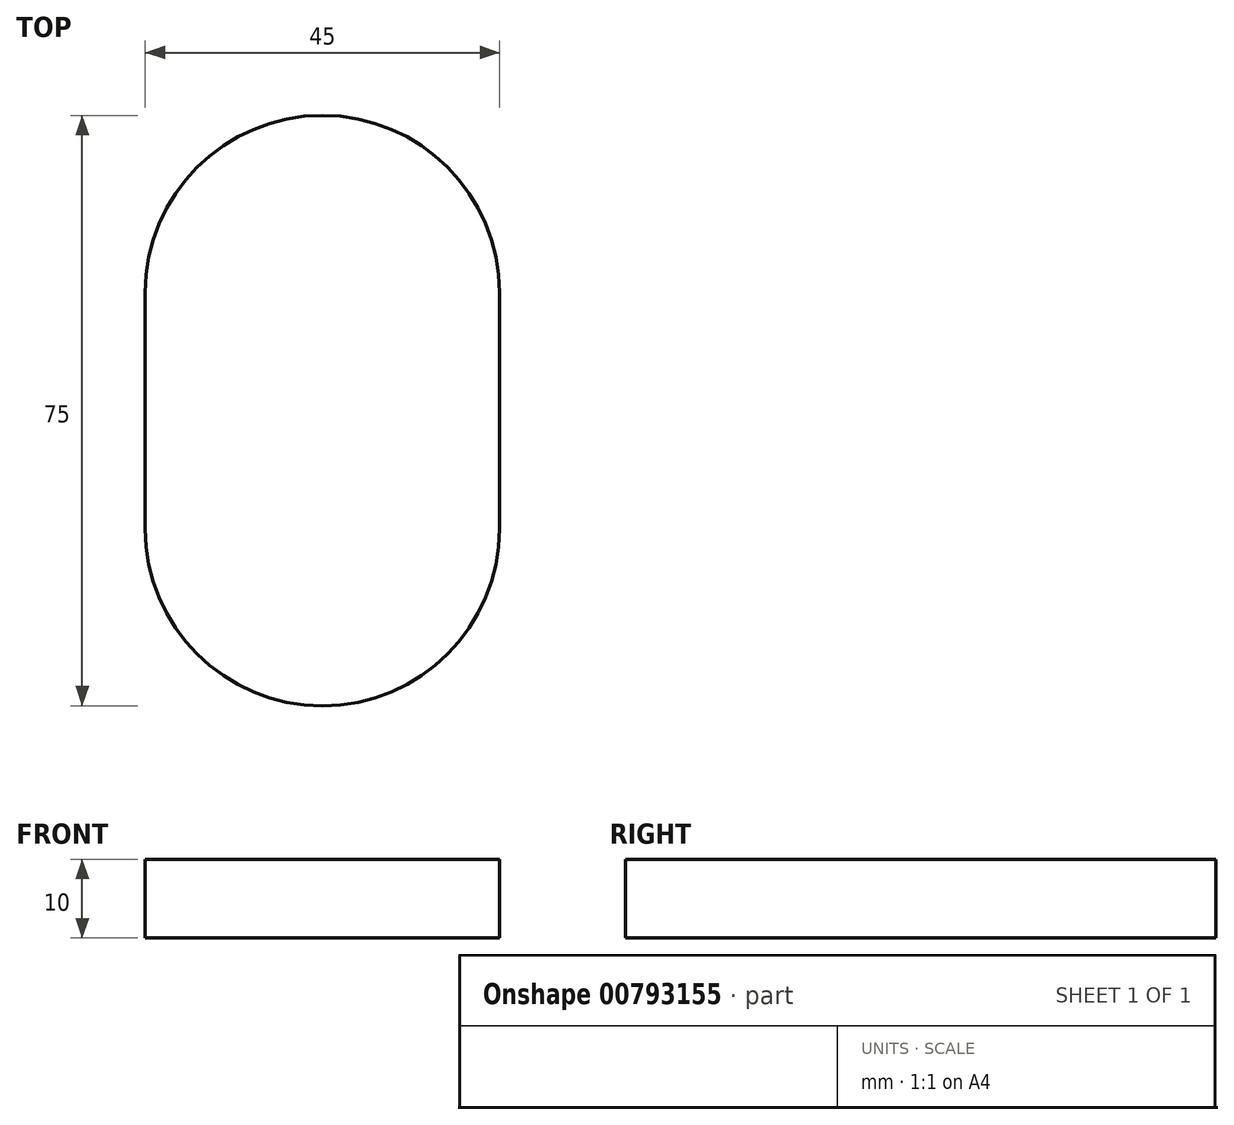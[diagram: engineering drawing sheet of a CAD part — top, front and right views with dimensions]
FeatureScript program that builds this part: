
annotation { "Feature Type Name" : "Feature", "Feature Type Description" : "" }
export const myFeature = defineFeature(function(context is Context, id is Id, definition is map)
    precondition{}
    {
        {
            var Q0;
            Q0=qCreatedBy(makeId("Top.planeOp"),FACE);
            var sketch = newSketch(context, id + "F0", { "sketchPlane" : qUnion([Q0])});
            skLineSegment(sketch, "E0", {"start": v(0, 15) * mm, "end": v(0, -15) * mm, "construction": true});
            skArc(sketch, "E1.0.startCap", {"start": v(-22.5, 15) * mm, "mid": v(0, 37.5) * mm, "end": v(22.5, 15) * mm});
            skArc(sketch, "E1.0.endCap", {"start": v(22.5, -15) * mm, "mid": v(0, -37.5) * mm, "end": v(-22.5, -15) * mm});
            skLineSegment(sketch, "E1.0.left", {"start": v(22.5, 15) * mm, "end": v(22.5, -15) * mm});
            skLineSegment(sketch, "E1.0.right", {"start": v(-22.5, 15) * mm, "end": v(-22.5, -15) * mm});
            skLineSegment(sketch, "E2.bottom", {"start": v(57.5, 80) * mm, "end": v(-57.5, 80) * mm});
            skLineSegment(sketch, "E2.top", {"start": v(57.5, -80) * mm, "end": v(-57.5, -80) * mm});
            skLineSegment(sketch, "E2.left", {"start": v(57.5, 80) * mm, "end": v(57.5, -80) * mm});
            skLineSegment(sketch, "E2.right", {"start": v(-57.5, 80) * mm, "end": v(-57.5, -80) * mm});
            skPoint(sketch, "E2.middle", {"position": v(0, 0) * mm});
            skSolve(sketch);
        }
        {
            var Q0;
            Q0=makeQuery(id+"F0.imprint","IMPRINT",FACE,{"disambiguationData":[TD([[makeQuery(id+"F0.imprint","IMPRINT",EDGE,{"derivedFrom":sQuery(id+"F0.wireOp",EDGE,"E1.0.startCap")}),1.0]])]});
            extrude(context, id + "F1", {"entities" : qUnion([Q0]), "depth" : 10 * mm, "offsetDistance" : 25 * mm});
        }
        {
            var Q0;
            Q0=makeQuery(id+"F1.opExtrude","CAP_FACE",FACE,{"disambiguationData":[OSD([sQuery(id+"F0.wireOp",EDGE,"E1.0.startCap"),sQuery(id+"F0.wireOp",EDGE,"E1.0.endCap"),sQuery(id+"F0.wireOp",EDGE,"E1.0.left"),sQuery(id+"F0.wireOp",EDGE,"E1.0.right"),sQuery(id+"F0.wireOp",EDGE,"E2.bottom"),sQuery(id+"F0.wireOp",EDGE,"E2.top"),sQuery(id+"F0.wireOp",EDGE,"E2.left"),sQuery(id+"F0.wireOp",EDGE,"E2.right")])],"isStart":false});
            var sketch = newSketch(context, id + "F2", { "sketchPlane" : qUnion([Q0])});
            skLineSegment(sketch, "E3", {"start": v(-30, 15) * mm, "end": v(-30, -15) * mm});
            skLineSegment(sketch, "E4", {"start": v(-30, 0) * mm, "end": v(0, 0) * mm});
            skArc(sketch, "E5.0.startCap", {"start": v(-34, 15) * mm, "mid": v(-30, 19) * mm, "end": v(-26, 15) * mm});
            skArc(sketch, "E5.0.endCap", {"start": v(-26, -15) * mm, "mid": v(-30, -19) * mm, "end": v(-34, -15) * mm});
            skLineSegment(sketch, "E5.0.left", {"start": v(-26, 15) * mm, "end": v(-26, -15) * mm});
            skLineSegment(sketch, "E5.0.right", {"start": v(-34, 15) * mm, "end": v(-34, -15) * mm});
            skSolve(sketch);
        }
        {
            var Q0;
            Q0 = qSketchRegion(id + "F2", true);
            extrude(context, id + "F3", {"entities" : qUnion([Q0]), "operationType" : NewBodyOperationType.REMOVE, "endBound" : BoundingType.THROUGH_ALL, "oppositeDirection" : true, "depth" : 25 * mm, "offsetDistance" : 25 * mm});
        }
    });
